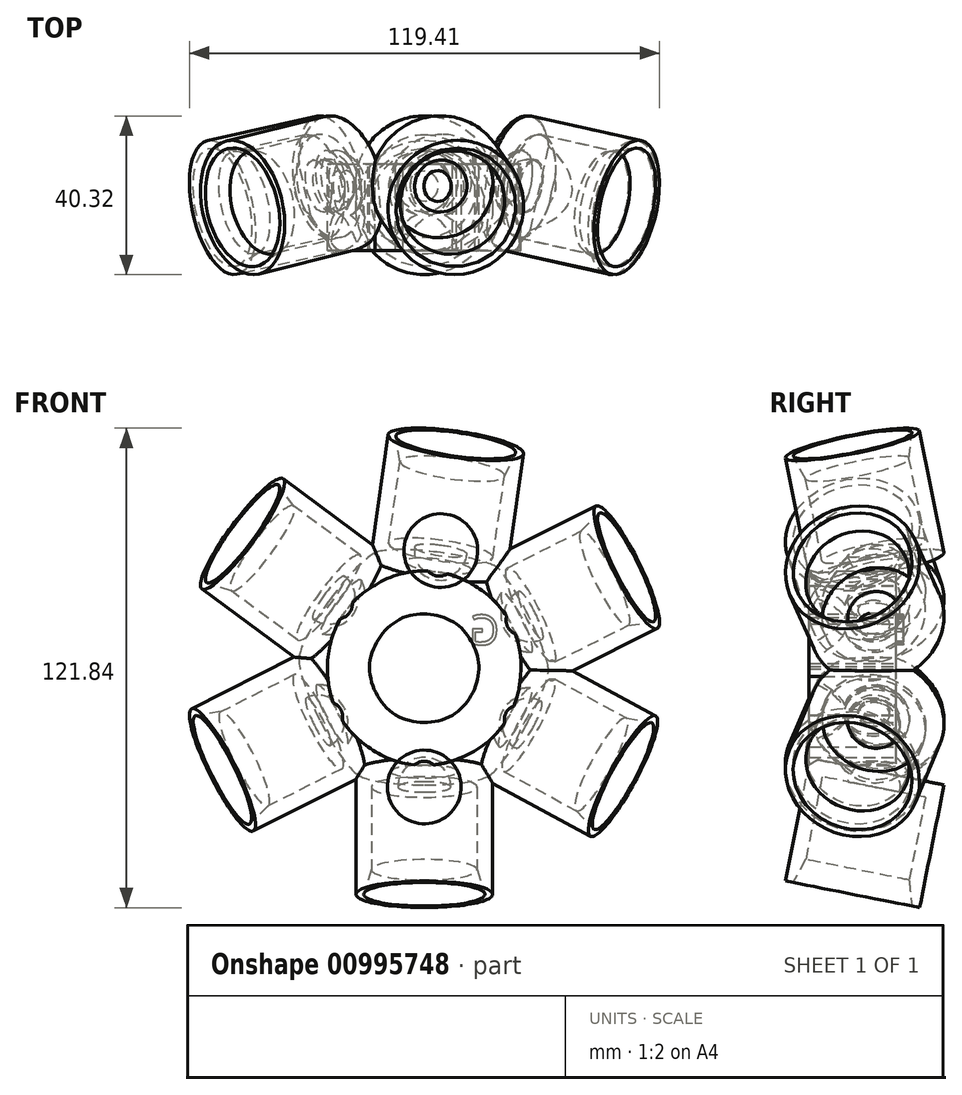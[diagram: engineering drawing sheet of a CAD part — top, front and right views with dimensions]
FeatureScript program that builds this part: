
annotation { "Feature Type Name" : "Feature", "Feature Type Description" : "" }
export const myFeature = defineFeature(function(context is Context, id is Id, definition is map)
    precondition{}
    {
        {
            var Q0;
            Q0=qCreatedBy(makeId("Front.planeOp"),FACE);
            var sketch = newSketch(context, id + "F0", { "sketchPlane" : qUnion([Q0])});
            skPoint(sketch, "E0.middle", {"position": v(0, 0) * mm});
            skPoint(sketch, "E1", {"position": v(0, 43.11) * mm});
            skCircle(sketch, "E2", {"center": v(0, 43.11) * mm, "radius": 23.5 * mm});
            skCircle(sketch, "E3", {"center": v(0, 43.11) * mm, "radius": 15 * mm});
            skLineSegment(sketch, "E4", {"start": v(0, 77.35) * mm, "end": v(0, -6.47) * mm, "construction": true});
            skPoint(sketch, "E5", {"position": v(0, 19.61) * mm});
            skLineSegment(sketch, "E6", {"start": v(26.39, 19.61) * mm, "end": v(-30.99, 19.61) * mm, "construction": true});
            skSolve(sketch);
        }
        {
            var Q0;
            Q0=sQuery(id+"F0.wireOp",EDGE,"E6");
            cPlane(context, id + "F1", {"entities" : qUnion([Q0]), "cplaneType" : CPlaneType.LINE_ANGLE, "offset" : 25 * mm, "angle" : 11.25 * degree, "width" : 150 * mm, "height" : 150 * mm});
        }
        {
            var Q0;
            Q0=qCreatedBy(id+"F1.planeOp",FACE);
            var sketch = newSketch(context, id + "F2", { "sketchPlane" : qUnion([Q0])});
            skPoint(sketch, "E7.middle", {"position": v(-6.69, -12.3) * mm});
            skLineSegment(sketch, "E8", {"start": v(8.7, -27.2) * mm, "end": v(10.7, -27.2) * mm});
            skPoint(sketch, "E9.end.orphan", {"position": v(6.7, -27.2) * mm});
            skPoint(sketch, "E10", {"position": v(-6.69, 29.59) * mm});
            skLineSegment(sketch, "E11.right", {"start": v(13.39, 11.2) * mm, "end": v(13.39, -10.25) * mm});
            skArc(sketch, "E12", {"start": v(6.73, 11.2) * mm, "mid": v(4.76, 15.95) * mm, "end": v(0, 17.92) * mm});
            skArc(sketch, "E13", {"start": v(8.47, 15.2) * mm, "mid": v(5.01, 19.1) * mm, "end": v(0, 20.56) * mm});
            skLineSegment(sketch, "E14", {"start": v(17.39, 15.2) * mm, "end": v(17.39, -16.6) * mm});
            skLineSegment(sketch, "E15", {"start": v(15.39, -16.6) * mm, "end": v(17.39, -16.6) * mm});
            skLineSegment(sketch, "E16", {"start": v(17.39, 15.2) * mm, "end": v(8.47, 15.2) * mm});
            skLineSegment(sketch, "E17", {"start": v(15.39, -16.6) * mm, "end": v(13.39, -10.25) * mm});
            skLineSegment(sketch, "E18", {"start": v(13.39, 11.2) * mm, "end": v(6.73, 11.2) * mm});
            skLineSegment(sketch, "E19", {"start": v(0, 17.92) * mm, "end": v(0, 20.56) * mm});
            skSolve(sketch);
        }
        {
            var Q0;
            Q0=makeQuery(id+"F2.imprint","IMPRINT",FACE,{"disambiguationData":[TD([[makeQuery(id+"F2.imprint","IMPRINT",EDGE,{"derivedFrom":sQuery(id+"F2.wireOp",EDGE,"E11.right")}),1.0]])]});
            var Q1;
            Q1=sQuery(id+"F2.wireOp",EDGE,"E19");
            revolve(context, id + "F3", {"surfaceOperationType" : NewSurfaceOperationType.NEW, "entities" : qUnion([Q0]), "axis" : qUnion([Q1]), "revolveType" : RevolveType.FULL});
        }
        {
            var Q0;
            Q0=makeQuery(id+"F0.imprint","IMPRINT",FACE,{"disambiguationData":[TD([[makeQuery(id+"F0.imprint","IMPRINT",EDGE,{"derivedFrom":sQuery(id+"F0.wireOp",EDGE,"E2")}),1.0]])]});
            extrude(context, id + "F4", {"entities" : qUnion([Q0]), "operationType" : NewBodyOperationType.ADD, "depth" : 18 * mm, "offsetDistance" : 25 * mm, "hasSecondDirection" : true, "secondDirectionOppositeDirection" : true, "secondDirectionDepth" : 4 * mm});
        }
        {
            var Q0;
            Q0=qCreatedBy(makeId("Right.planeOp"),FACE);
            var sketch = newSketch(context, id + "F5", { "sketchPlane" : qUnion([Q0])});
            skLineSegment(sketch, "E20", {"start": v(-35.17, 41.9) * mm, "end": v(25.33, 41.9) * mm, "construction": true});
            skSolve(sketch);
        }
        {
            var Q0;
            Q0=makeQuery(id+"F3.opRevolve","SWEPT_BODY",BODY,{"disambiguationData":[OSD([sQuery(id+"F2.wireOp",EDGE,"E11.right"),sQuery(id+"F2.wireOp",EDGE,"E12"),sQuery(id+"F2.wireOp",EDGE,"E13"),sQuery(id+"F2.wireOp",EDGE,"E14"),sQuery(id+"F2.wireOp",EDGE,"E15"),sQuery(id+"F2.wireOp",EDGE,"E16"),sQuery(id+"F2.wireOp",EDGE,"E17"),sQuery(id+"F2.wireOp",EDGE,"E18"),sQuery(id+"F2.wireOp",EDGE,"E19")])]});
            var Q1;
            Q1=sQuery(id+"F5.wireOp",EDGE,"E20");
            circularPattern(context, id + "F6", {"entities" : qUnion([Q0]), "axis" : qUnion([Q1]), "angle" : 63.25 * degree, "instanceCount" : 2});
        }
        {
            var Q0;
            Q0=makeQuery(id+"F3.opRevolve","SWEPT_BODY",BODY,{"disambiguationData":[OSD([sQuery(id+"F2.wireOp",EDGE,"E11.right"),sQuery(id+"F2.wireOp",EDGE,"E12"),sQuery(id+"F2.wireOp",EDGE,"E13"),sQuery(id+"F2.wireOp",EDGE,"E14"),sQuery(id+"F2.wireOp",EDGE,"E15"),sQuery(id+"F2.wireOp",EDGE,"E16"),sQuery(id+"F2.wireOp",EDGE,"E17"),sQuery(id+"F2.wireOp",EDGE,"E18"),sQuery(id+"F2.wireOp",EDGE,"E19")])]});
            var Q1;
            Q1=sQuery(id+"F5.wireOp",EDGE,"E20");
            circularPattern(context, id + "F7", {"entities" : qUnion([Q0]), "axis" : qUnion([Q1]), "angle" : 61.5 * degree, "instanceCount" : 2, "oppositeDirection" : true});
        }
        {
            var Q0;
            Q0=makeQuery(id+"F3.opRevolve","SWEPT_BODY",BODY,{"disambiguationData":[OSD([sQuery(id+"F2.wireOp",EDGE,"E11.right"),sQuery(id+"F2.wireOp",EDGE,"E12"),sQuery(id+"F2.wireOp",EDGE,"E13"),sQuery(id+"F2.wireOp",EDGE,"E14"),sQuery(id+"F2.wireOp",EDGE,"E15"),sQuery(id+"F2.wireOp",EDGE,"E16"),sQuery(id+"F2.wireOp",EDGE,"E17"),sQuery(id+"F2.wireOp",EDGE,"E18"),sQuery(id+"F2.wireOp",EDGE,"E19")])]});
            var Q1;
            Q1=sQuery(id+"F5.wireOp",EDGE,"E20");
            circularPattern(context, id + "F8", {"entities" : qUnion([Q0]), "axis" : qUnion([Q1]), "angle" : 116.5 * degree, "instanceCount" : 2, "oppositeDirection" : true, "equalSpace" : true});
        }
        {
            var Q0;
            Q0=makeQuery(id+"F3.opRevolve","SWEPT_BODY",BODY,{"disambiguationData":[OSD([sQuery(id+"F2.wireOp",EDGE,"E11.right"),sQuery(id+"F2.wireOp",EDGE,"E12"),sQuery(id+"F2.wireOp",EDGE,"E13"),sQuery(id+"F2.wireOp",EDGE,"E14"),sQuery(id+"F2.wireOp",EDGE,"E15"),sQuery(id+"F2.wireOp",EDGE,"E16"),sQuery(id+"F2.wireOp",EDGE,"E17"),sQuery(id+"F2.wireOp",EDGE,"E18"),sQuery(id+"F2.wireOp",EDGE,"E19")])]});
            var Q1;
            Q1=sQuery(id+"F5.wireOp",EDGE,"E20");
            circularPattern(context, id + "F9", {"entities" : qUnion([Q0]), "axis" : qUnion([Q1]), "angle" : 188 * degree, "instanceCount" : 2, "equalSpace" : true});
        }
        {
            var Q0;
            Q0=makeQuery(id+"F3.opRevolve","SWEPT_BODY",BODY,{"disambiguationData":[OSD([sQuery(id+"F2.wireOp",EDGE,"E11.right"),sQuery(id+"F2.wireOp",EDGE,"E12"),sQuery(id+"F2.wireOp",EDGE,"E13"),sQuery(id+"F2.wireOp",EDGE,"E14"),sQuery(id+"F2.wireOp",EDGE,"E15"),sQuery(id+"F2.wireOp",EDGE,"E16"),sQuery(id+"F2.wireOp",EDGE,"E17"),sQuery(id+"F2.wireOp",EDGE,"E18"),sQuery(id+"F2.wireOp",EDGE,"E19")])]});
            var Q1;
            Q1=sQuery(id+"F5.wireOp",EDGE,"E20");
            circularPattern(context, id + "F10", {"entities" : qUnion([Q0]), "axis" : qUnion([Q1]), "angle" : 126.5 * degree, "instanceCount" : 2, "equalSpace" : true});
        }
        {
            var Q0;
            Q0=makeQuery(id+"F3.opRevolve","SWEPT_BODY",BODY,{"disambiguationData":[OSD([sQuery(id+"F2.wireOp",EDGE,"E11.right"),sQuery(id+"F2.wireOp",EDGE,"E12"),sQuery(id+"F2.wireOp",EDGE,"E13"),sQuery(id+"F2.wireOp",EDGE,"E14"),sQuery(id+"F2.wireOp",EDGE,"E15"),sQuery(id+"F2.wireOp",EDGE,"E16"),sQuery(id+"F2.wireOp",EDGE,"E17"),sQuery(id+"F2.wireOp",EDGE,"E18"),sQuery(id+"F2.wireOp",EDGE,"E19")])]});
            var Q1;
            Q1=makeQuery(id+"F6.opPattern","COPY",BODY,{"derivedFrom":makeQuery(id+"F3.opRevolve","SWEPT_BODY",BODY,{"disambiguationData":[OSD([sQuery(id+"F2.wireOp",EDGE,"E11.right"),sQuery(id+"F2.wireOp",EDGE,"E12"),sQuery(id+"F2.wireOp",EDGE,"E13"),sQuery(id+"F2.wireOp",EDGE,"E14"),sQuery(id+"F2.wireOp",EDGE,"E15"),sQuery(id+"F2.wireOp",EDGE,"E16"),sQuery(id+"F2.wireOp",EDGE,"E17"),sQuery(id+"F2.wireOp",EDGE,"E18"),sQuery(id+"F2.wireOp",EDGE,"E19")])]}),"instanceName":"1"});
            var Q2;
            Q2=makeQuery(id+"F8.opPattern","COPY",BODY,{"derivedFrom":makeQuery(id+"F3.opRevolve","SWEPT_BODY",BODY,{"disambiguationData":[OSD([sQuery(id+"F2.wireOp",EDGE,"E11.right"),sQuery(id+"F2.wireOp",EDGE,"E12"),sQuery(id+"F2.wireOp",EDGE,"E13"),sQuery(id+"F2.wireOp",EDGE,"E14"),sQuery(id+"F2.wireOp",EDGE,"E15"),sQuery(id+"F2.wireOp",EDGE,"E16"),sQuery(id+"F2.wireOp",EDGE,"E17"),sQuery(id+"F2.wireOp",EDGE,"E18"),sQuery(id+"F2.wireOp",EDGE,"E19")])]}),"instanceName":"1"});
            var Q3;
            Q3=makeQuery(id+"F9.opPattern","COPY",BODY,{"derivedFrom":makeQuery(id+"F3.opRevolve","SWEPT_BODY",BODY,{"disambiguationData":[OSD([sQuery(id+"F2.wireOp",EDGE,"E11.right"),sQuery(id+"F2.wireOp",EDGE,"E12"),sQuery(id+"F2.wireOp",EDGE,"E13"),sQuery(id+"F2.wireOp",EDGE,"E14"),sQuery(id+"F2.wireOp",EDGE,"E15"),sQuery(id+"F2.wireOp",EDGE,"E16"),sQuery(id+"F2.wireOp",EDGE,"E17"),sQuery(id+"F2.wireOp",EDGE,"E18"),sQuery(id+"F2.wireOp",EDGE,"E19")])]}),"instanceName":"1"});
            var Q4;
            Q4=makeQuery(id+"F10.opPattern","COPY",BODY,{"derivedFrom":makeQuery(id+"F3.opRevolve","SWEPT_BODY",BODY,{"disambiguationData":[OSD([sQuery(id+"F2.wireOp",EDGE,"E11.right"),sQuery(id+"F2.wireOp",EDGE,"E12"),sQuery(id+"F2.wireOp",EDGE,"E13"),sQuery(id+"F2.wireOp",EDGE,"E14"),sQuery(id+"F2.wireOp",EDGE,"E15"),sQuery(id+"F2.wireOp",EDGE,"E16"),sQuery(id+"F2.wireOp",EDGE,"E17"),sQuery(id+"F2.wireOp",EDGE,"E18"),sQuery(id+"F2.wireOp",EDGE,"E19")])]}),"instanceName":"1"});
            var Q5;
            Q5=makeQuery(id+"F7.opPattern","COPY",BODY,{"derivedFrom":makeQuery(id+"F3.opRevolve","SWEPT_BODY",BODY,{"disambiguationData":[OSD([sQuery(id+"F2.wireOp",EDGE,"E11.right"),sQuery(id+"F2.wireOp",EDGE,"E12"),sQuery(id+"F2.wireOp",EDGE,"E13"),sQuery(id+"F2.wireOp",EDGE,"E14"),sQuery(id+"F2.wireOp",EDGE,"E15"),sQuery(id+"F2.wireOp",EDGE,"E16"),sQuery(id+"F2.wireOp",EDGE,"E17"),sQuery(id+"F2.wireOp",EDGE,"E18"),sQuery(id+"F2.wireOp",EDGE,"E19")])]}),"instanceName":"1"});
            booleanBodies(context, id + "F11", {"operationType" : BooleanOperationType.UNION, "tools" : qUnion([Q0, Q1, Q2, Q3, Q4, Q5])});
        }
        {
            var Q0;
            {var subQ0=makeQuery(id+"F4.opExtrude","CAP_FACE",FACE,{"disambiguationData":[OSD([sQuery(id+"F0.wireOp",EDGE,"E2"),sQuery(id+"F0.wireOp",EDGE,"E3")])],"isStart":true});Q0=makeQuery(id+"F11.opBoolean","MERGE",FACE,{"derivedFrom":[subQ0,makeQuery(id+"F6.opPattern","COPY",FACE,{"derivedFrom":subQ0,"instanceName":"1"}),makeQuery(id+"F7.opPattern","COPY",FACE,{"derivedFrom":subQ0,"instanceName":"1"}),makeQuery(id+"F8.opPattern","COPY",FACE,{"derivedFrom":subQ0,"instanceName":"1"}),makeQuery(id+"F9.opPattern","COPY",FACE,{"derivedFrom":subQ0,"instanceName":"1"}),makeQuery(id+"F10.opPattern","COPY",FACE,{"derivedFrom":subQ0,"instanceName":"1"})]});}
            cPlane(context, id + "F12", {"entities" : qUnion([Q0]), "cplaneType" : CPlaneType.OFFSET, "offset" : 0 * mm, "width" : 150 * mm, "height" : 150 * mm});
        }
        {
            var Q0;
            Q0=qCreatedBy(id+"F12.planeOp",FACE);
            var sketch = newSketch(context, id + "F13", { "sketchPlane" : qUnion([Q0])});
            skText(sketch, "E21", { "text": "G", "fontName": "OpenSans-Regular.ttf"});
            const initialGuessF13  = {"E21": [-0.01906, 0.0479, 1, 0, 0.00756]};
            skSetInitialGuess(sketch, initialGuessF13);
            skSolve(sketch);
        }
        {
            var Q0;
            Q0=makeQuery(id+"F13.imprint","IMPRINT",FACE,{"disambiguationData":[TD([[makeQuery(id+"F13.imprint","IMPRINT",EDGE,{"derivedFrom":sQuery(id+"F13.wireOp",EDGE,"E21.sketch_text.stroke-0")}),-1.0]])]});
            extrude(context, id + "F14", {"entities" : qUnion([Q0]), "operationType" : NewBodyOperationType.ADD, "depth" : 2 * mm, "offsetDistance" : 25 * mm});
        }
    });
